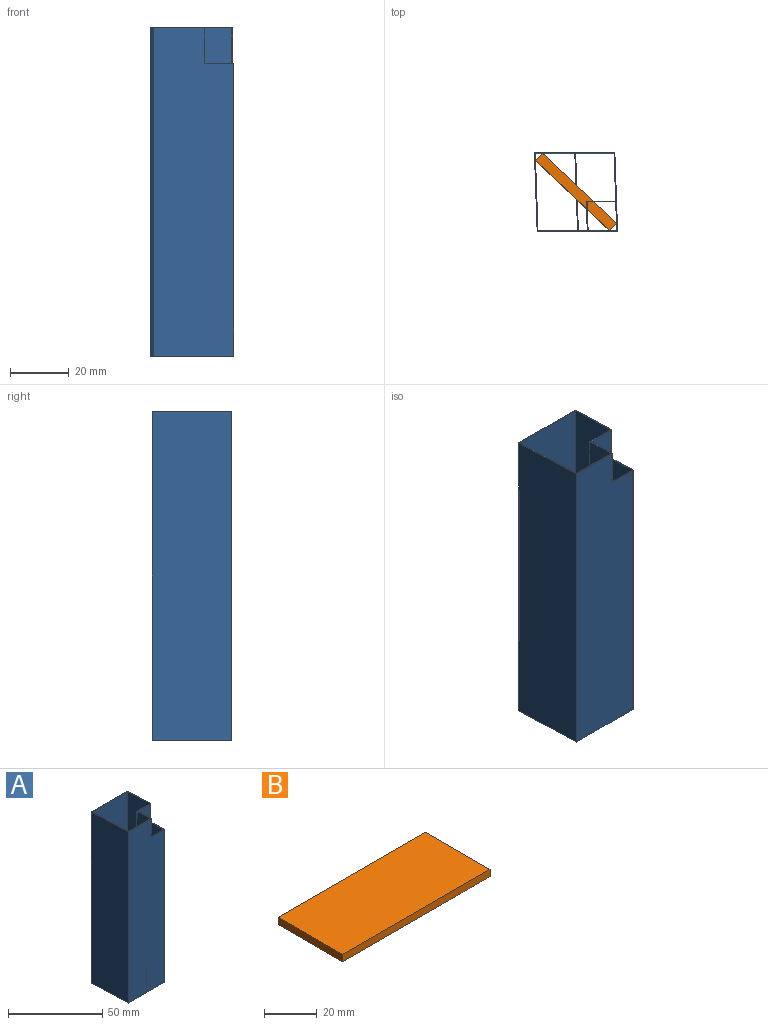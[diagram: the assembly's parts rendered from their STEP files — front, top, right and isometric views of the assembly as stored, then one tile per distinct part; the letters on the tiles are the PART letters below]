
ASSEMBLY  parts=2 mates=1
PART A: 21 faces, bbox 28.3x26.9x111.4 mm
  f0: plane 27.91x26.9mm, normal (0,0,1), area 32.2mm2, adj f1,f2,f3,f4,f5,f6,f7,f8
  f1: plane 111.4x26.3mm, normal (-1,-0.03,0), area 2811.7mm2, adj f0,f2,f7,f9,f16,f17,f18,f19
  f2: plane 111.4x26.72mm, normal (0,-1,0), area 2971.7mm2, adj f0,f1,f6,f9,f10,f12,f13
  f3: plane 111.4x27.32mm, normal (0,1,0), area 3043.1mm2, adj f0,f4,f8,f9
  f4: plane 111.4x26.9mm, normal (-1,-0.03,0), area 2998.5mm2, adj f0,f3,f5,f9
  f5: plane 111.4x27.32mm, normal (0,-1,0), area 2923mm2, adj f0,f4,f8,f9,f15,f19
  f6: plane 111.4x26.3mm, normal (1,0.03,0), area 2931.6mm2, adj f0,f2,f7,f9
  f7: plane 111.4x26.72mm, normal (0,1,0), area 2856.1mm2, adj f0,f1,f6,f9,f14,f18,f19
  f8: plane 111.4x26.9mm, normal (1,0.03,0), area 2878.5mm2, adj f0,f3,f5,f9,f19,f20
  f9: plane 28.26x26.9mm, normal (0,0,-1), area 40.1mm2, adj f1,f2,f3,f4,f5,f6,f7,f8
  f10: plane 26.28x15mm, normal (1,0.03,0), area 394.5mm2, adj f2,f9,f11,f13
  f11: plane 15x0.3mm, normal (0,-1,0), area 4.5mm2, adj f9,f10,f12,f13
  f12: plane 26.28x15mm, normal (-1,-0.03,0), area 394.5mm2, adj f2,f9,f11,f13
  f13: plane 26.28x1.22mm, normal (0,0,1), area 7.9mm2, adj f2,f10,f11,f12
  f14: plane 12x9.99mm, normal (-1,-0.03,0), area 120mm2, adj f0,f7,f17,f18
  f15: plane 12x9.99mm, normal (1,0.03,0), area 120mm2, adj f0,f5,f16,f18,f19
  f16: plane 12x9.71mm, normal (0,-1,0), area 116.5mm2, adj f0,f1,f15,f18
  f17: plane 12x10.01mm, normal (0,1,0), area 120.1mm2, adj f0,f1,f14,f18
  f18: plane 10.02x9.99mm, normal (0,0,-1), area 5.9mm2, adj f1,f7,f14,f15,f16,f17
  f19: plane 10.02x9.99mm, normal (0,0,1), area 5.9mm2, adj f1,f5,f7,f8,f15,f20
  f20: plane 12x0.3mm, normal (0.03,-1,0), area 3.6mm2, adj f0,f1,f8,f19
PART B: 6 faces, bbox 79x34.6x3.4 mm
  f0: plane 79x3.4mm, normal (0,1,0), area 268.6mm2, adj f1,f3,f4,f5
  f1: plane 34.6x3.4mm, normal (-1,0,0), area 117.6mm2, adj f0,f2,f4,f5
  f2: plane 79x3.4mm, normal (0,-1,0), area 268.6mm2, adj f1,f3,f4,f5
  f3: plane 34.6x3.4mm, normal (1,0,0), area 117.6mm2, adj f0,f2,f4,f5
  f4: plane 79x34.6mm, normal (0,0,1), area 2733.4mm2, adj f0,f1,f2,f3
  f5: plane 79x34.6mm, normal (0,0,-1), area 2733.4mm2, adj f0,f1,f2,f3
PLACE A t=(11.92,12.68,57.69)mm fixed
PLACE B rot(axis=(0.68,0.29,-0.68),147.5deg) t=(13.09,13.93,112.19)mm
MATE planar B.f3 <-> A.f13  axis (0,0,-1) through (11.92,12.7,72.69)mm
